# Revit family: NU-340 AireGard Horizontal Laminar Flow Clean Workstation With Castors
name_source: partatom
category: Mechanical Equipment
units: mm (PartAtom-declared; Revit-internal decimal feet)

## family parameters
Always vertical = Yes
Cut with Voids When Loaded = No
OmniClass Number = 23.75.00.00
OmniClass Title = Climate Control (HVAC)
Part Type = Normal
Room Calculation Point = No
Round Connector Dimension = Use Diameter
Shared = No
Work Plane-Based = No

## types (8) — shared parameters
Default Elevation = 0' - 0"
Depth = 2' - 8"
Description = Horizontal Airflow Console
Manufacturer = Nuaire Inc.

## per-type parameters (varying)
| type | CASTOR DIM 1 | CASTOR DIM 2 | Cabinet_Height | Model | Width | Workzone_Height |
| NU-340-430 | 1' - 11 1/4" | 1' - 10" | 3' - 6" | NU-340-330 | 4' - 2" | 2' - 8" |
| NU-340-436 | 1' - 11 1/4" | 1' - 10" | 4' - 0" | NU-340-436 | 4' - 2" | 3' - 2" |
| NU-340-336 | 1' - 5 1/4" | 1' - 4" | 4' - 0" | NU-340-336 | 3' - 2" | 3' - 2" |
| NU-340-330 | 1' - 5 1/4" | 1' - 4" | 3' - 6" | NU-340-330 | 3' - 2" | 2' - 8" |
| NU-340-536 | 2' - 5 1/4" | 2' - 4" | 4' - 0" | NU-340-536 | 5' - 2" | 3' - 2" |
| NU-340-636 | 2' - 11 1/4" | 2' - 10" | 4' - 0" | NU-340-636 | 6' - 2" | 3' - 2" |
| NU-340-530 | 2' - 5 1/4" | 2' - 4" | 3' - 6" | NU-340-530 | 5' - 2" | 2' - 8" |
| NU-340-630 | 2' - 11 1/4" | 2' - 10" | 3' - 6" | NU-340-630 | 6' - 2" | 2' - 8" |

## geometry (parser evidence)
native form markers: Sweep x3
no freeform markers — native parametric forms only
